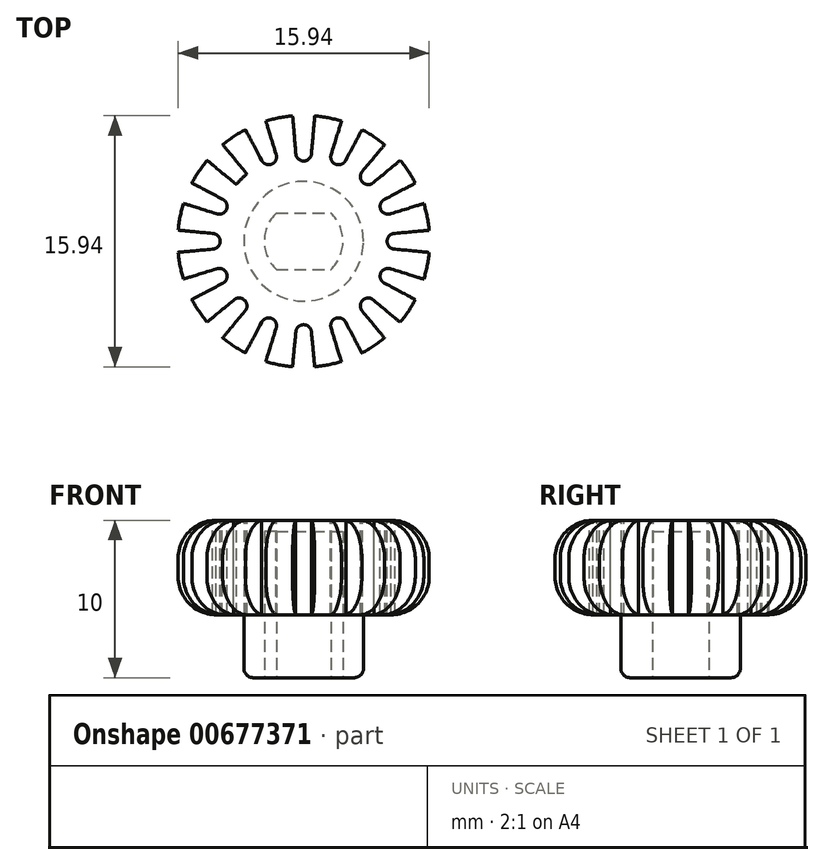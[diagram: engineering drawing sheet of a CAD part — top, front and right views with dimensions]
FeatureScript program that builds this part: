
annotation { "Feature Type Name" : "Feature", "Feature Type Description" : "" }
export const myFeature = defineFeature(function(context is Context, id is Id, definition is map)
    precondition{}
    {
        {
            var Q0;
            Q0=qCreatedBy(makeId("Front.planeOp"),FACE);
            var sketch = newSketch(context, id + "F0", { "sketchPlane" : qUnion([Q0])});
            skLineSegment(sketch, "E0", {"start": v(0, 0) * mm, "end": v(3.8, 0) * mm});
            skLineSegment(sketch, "E1", {"start": v(3.8, 0) * mm, "end": v(3.8, 4) * mm});
            skLineSegment(sketch, "E2", {"start": v(3.8, 4) * mm, "end": v(5.6, 4) * mm});
            skLineSegment(sketch, "E3", {"start": v(8, 6.4) * mm, "end": v(8, 7.6) * mm});
            skLineSegment(sketch, "E4", {"start": v(5.6, 10) * mm, "end": v(0, 10) * mm});
            skLineSegment(sketch, "E5", {"start": v(0, 10) * mm, "end": v(0, 0) * mm});
            skPoint(sketch, "E6.visualSharp", {"position": v(8, 10) * mm});
            skArc(sketch, "E6.filletArc", {"start": v(8, 7.6) * mm, "mid": v(7.3, 9.3) * mm, "end": v(5.6, 10) * mm});
            skPoint(sketch, "E7.visualSharp", {"position": v(8, 4) * mm});
            skArc(sketch, "E7.filletArc", {"start": v(5.6, 4) * mm, "mid": v(7.3, 4.7) * mm, "end": v(8, 6.4) * mm});
            skSolve(sketch);
        }
        {
            var Q0;
            Q0=makeQuery(id+"F0.imprint","IMPRINT",FACE,{"disambiguationData":[TD([[makeQuery(id+"F0.imprint","IMPRINT",EDGE,{"derivedFrom":sQuery(id+"F0.wireOp",EDGE,"E0")}),1.0]])]});
            var Q1;
            Q1=sQuery(id+"F0.wireOp",EDGE,"E5");
            revolve(context, id + "F1", {"entities" : qUnion([Q0]), "axis" : qUnion([Q1]), "revolveType" : RevolveType.FULL});
        }
        {
            var Q0;
            Q0=makeQuery(id+"F1.opRevolve","SWEPT_FACE",FACE,{"disambiguationData":[OSD([sQuery(id+"F0.wireOp",EDGE,"E0")])]});
            var sketch = newSketch(context, id + "F2", { "sketchPlane" : qUnion([Q0])});
            skLineSegment(sketch, "E8", {"start": v(-1.73, 1.8) * mm, "end": v(1.73, 1.8) * mm});
            skLineSegment(sketch, "E9", {"start": v(-1.73, -1.8) * mm, "end": v(1.73, -1.8) * mm});
            skArc(sketch, "E10", {"start": v(-1.73, 1.8) * mm, "mid": v(-2.5, 0) * mm, "end": v(-1.73, -1.8) * mm});
            skArc(sketch, "E11.trimOffspring", {"start": v(1.73, -1.8) * mm, "mid": v(2.5, 0) * mm, "end": v(1.73, 1.8) * mm});
            skPoint(sketch, "E12.orphan", {"position": v(3.04, 1.8) * mm});
            skPoint(sketch, "E13.orphan", {"position": v(2.98, -1.8) * mm});
            skSolve(sketch);
        }
        {
            var Q0;
            Q0=makeQuery(id+"F2.imprint","IMPRINT",FACE,{"disambiguationData":[TD([[makeQuery(id+"F2.imprint","IMPRINT",EDGE,{"derivedFrom":sQuery(id+"F2.wireOp",EDGE,"E8")}),-1.0]])]});
            extrude(context, id + "F3", {"entities" : qUnion([Q0]), "operationType" : NewBodyOperationType.REMOVE, "oppositeDirection" : true, "depth" : 9.3 * mm, "offsetDistance" : 25 * mm});
        }
        {
            var Q0;
            Q0=makeQuery(id+"F1.opRevolve","SWEPT_FACE",FACE,{"disambiguationData":[OSD([sQuery(id+"F0.wireOp",EDGE,"E4")])]});
            var sketch = newSketch(context, id + "F4", { "sketchPlane" : qUnion([Q0])});
            skLineSegment(sketch, "E14", {"start": v(-0.7, 7.97) * mm, "end": v(-0.5, 5.6) * mm});
            skArc(sketch, "E15", {"start": v(-0.5, 5.6) * mm, "mid": v(0, 5.1) * mm, "end": v(0.5, 5.6) * mm});
            skPoint(sketch, "E16.orphan", {"position": v(0.5, 5.6) * mm});
            skLineSegment(sketch, "E17", {"start": v(0.5, 5.6) * mm, "end": v(0.7, 7.97) * mm});
            skPoint(sketch, "E18.1.0", {"position": v(-1.76, 5.55) * mm});
            skArc(sketch, "E18.1.1", {"start": v(-2.68, 5.17) * mm, "mid": v(-2.03, 4.9) * mm, "end": v(-1.76, 5.55) * mm});
            skLineSegment(sketch, "E18.1.2", {"start": v(-3.7, 7.1) * mm, "end": v(-2.68, 5.17) * mm});
            skLineSegment(sketch, "E18.1.3", {"start": v(-1.76, 5.55) * mm, "end": v(-2.4, 7.63) * mm});
            skArc(sketch, "E18.1.4", {"start": v(-2.4, 7.63) * mm, "mid": v(-3.06, 7.4) * mm, "end": v(-3.7, 7.1) * mm});
            skPoint(sketch, "E18.2.0", {"position": v(-3.75, 4.45) * mm});
            skArc(sketch, "E18.2.1", {"start": v(-4.45, 3.75) * mm, "mid": v(-3.75, 3.75) * mm, "end": v(-3.75, 4.45) * mm});
            skLineSegment(sketch, "E18.2.2", {"start": v(-6.13, 5.14) * mm, "end": v(-4.45, 3.75) * mm});
            skLineSegment(sketch, "E18.2.3", {"start": v(-3.75, 4.45) * mm, "end": v(-5.14, 6.13) * mm});
            skArc(sketch, "E18.2.4", {"start": v(-5.14, 6.13) * mm, "mid": v(-5.65, 5.66) * mm, "end": v(-6.13, 5.14) * mm});
            skPoint(sketch, "E18.3.0", {"position": v(-5.17, 2.68) * mm});
            skArc(sketch, "E18.3.1", {"start": v(-5.55, 1.76) * mm, "mid": v(-4.9, 2.03) * mm, "end": v(-5.17, 2.68) * mm});
            skLineSegment(sketch, "E18.3.2", {"start": v(-7.63, 2.4) * mm, "end": v(-5.55, 1.76) * mm});
            skLineSegment(sketch, "E18.3.3", {"start": v(-5.17, 2.68) * mm, "end": v(-7.1, 3.7) * mm});
            skArc(sketch, "E18.3.4", {"start": v(-7.1, 3.7) * mm, "mid": v(-7.39, 3.06) * mm, "end": v(-7.63, 2.4) * mm});
            skPoint(sketch, "E18.4.0", {"position": v(-5.8, 0.5) * mm});
            skArc(sketch, "E18.4.1", {"start": v(-5.8, -0.5) * mm, "mid": v(-5.3, 0) * mm, "end": v(-5.8, 0.5) * mm});
            skLineSegment(sketch, "E18.4.2", {"start": v(-7.97, -0.7) * mm, "end": v(-5.8, -0.5) * mm});
            skLineSegment(sketch, "E18.4.3", {"start": v(-5.8, 0.5) * mm, "end": v(-7.97, 0.7) * mm});
            skArc(sketch, "E18.4.4", {"start": v(-7.97, 0.7) * mm, "mid": v(-8, 0) * mm, "end": v(-7.97, -0.7) * mm});
            skPoint(sketch, "E18.5.0", {"position": v(-5.55, -1.76) * mm});
            skArc(sketch, "E18.5.1", {"start": v(-5.17, -2.68) * mm, "mid": v(-4.9, -2.03) * mm, "end": v(-5.55, -1.76) * mm});
            skLineSegment(sketch, "E18.5.2", {"start": v(-7.1, -3.7) * mm, "end": v(-5.17, -2.68) * mm});
            skLineSegment(sketch, "E18.5.3", {"start": v(-5.55, -1.76) * mm, "end": v(-7.63, -2.4) * mm});
            skArc(sketch, "E18.5.4", {"start": v(-7.63, -2.4) * mm, "mid": v(-7.4, -3.06) * mm, "end": v(-7.1, -3.7) * mm});
            skPoint(sketch, "E18.6.0", {"position": v(-4.45, -3.75) * mm});
            skArc(sketch, "E18.6.1", {"start": v(-3.75, -4.45) * mm, "mid": v(-3.75, -3.75) * mm, "end": v(-4.45, -3.75) * mm});
            skLineSegment(sketch, "E18.6.2", {"start": v(-5.14, -6.13) * mm, "end": v(-3.75, -4.45) * mm});
            skLineSegment(sketch, "E18.6.3", {"start": v(-4.45, -3.75) * mm, "end": v(-6.13, -5.14) * mm});
            skArc(sketch, "E18.6.4", {"start": v(-6.13, -5.14) * mm, "mid": v(-5.66, -5.65) * mm, "end": v(-5.14, -6.13) * mm});
            skPoint(sketch, "E18.7.0", {"position": v(-2.68, -5.17) * mm});
            skArc(sketch, "E18.7.1", {"start": v(-1.76, -5.55) * mm, "mid": v(-2.03, -4.9) * mm, "end": v(-2.68, -5.17) * mm});
            skLineSegment(sketch, "E18.7.2", {"start": v(-2.4, -7.63) * mm, "end": v(-1.76, -5.55) * mm});
            skLineSegment(sketch, "E18.7.3", {"start": v(-2.68, -5.17) * mm, "end": v(-3.7, -7.1) * mm});
            skArc(sketch, "E18.7.4", {"start": v(-3.7, -7.1) * mm, "mid": v(-3.06, -7.39) * mm, "end": v(-2.4, -7.63) * mm});
            skPoint(sketch, "E18.8.0", {"position": v(-0.5, -5.8) * mm});
            skArc(sketch, "E18.8.1", {"start": v(0.5, -5.8) * mm, "mid": v(0, -5.3) * mm, "end": v(-0.5, -5.8) * mm});
            skLineSegment(sketch, "E18.8.2", {"start": v(0.7, -7.97) * mm, "end": v(0.5, -5.8) * mm});
            skLineSegment(sketch, "E18.8.3", {"start": v(-0.5, -5.8) * mm, "end": v(-0.7, -7.97) * mm});
            skArc(sketch, "E18.8.4", {"start": v(-0.7, -7.97) * mm, "mid": v(0, -8) * mm, "end": v(0.7, -7.97) * mm});
            skPoint(sketch, "E18.9.0", {"position": v(1.76, -5.55) * mm});
            skArc(sketch, "E18.9.1", {"start": v(2.68, -5.17) * mm, "mid": v(2.03, -4.9) * mm, "end": v(1.76, -5.55) * mm});
            skLineSegment(sketch, "E18.9.2", {"start": v(3.7, -7.1) * mm, "end": v(2.68, -5.17) * mm});
            skLineSegment(sketch, "E18.9.3", {"start": v(1.76, -5.55) * mm, "end": v(2.4, -7.63) * mm});
            skArc(sketch, "E18.9.4", {"start": v(2.4, -7.63) * mm, "mid": v(3.06, -7.4) * mm, "end": v(3.7, -7.1) * mm});
            skPoint(sketch, "E18.10.0", {"position": v(3.75, -4.45) * mm});
            skArc(sketch, "E18.10.1", {"start": v(4.45, -3.75) * mm, "mid": v(3.75, -3.75) * mm, "end": v(3.75, -4.45) * mm});
            skLineSegment(sketch, "E18.10.2", {"start": v(6.13, -5.14) * mm, "end": v(4.45, -3.75) * mm});
            skLineSegment(sketch, "E18.10.3", {"start": v(3.75, -4.45) * mm, "end": v(5.14, -6.13) * mm});
            skArc(sketch, "E18.10.4", {"start": v(5.14, -6.13) * mm, "mid": v(5.65, -5.66) * mm, "end": v(6.13, -5.14) * mm});
            skPoint(sketch, "E18.11.0", {"position": v(5.17, -2.68) * mm});
            skArc(sketch, "E18.11.1", {"start": v(5.55, -1.76) * mm, "mid": v(4.9, -2.03) * mm, "end": v(5.17, -2.68) * mm});
            skLineSegment(sketch, "E18.11.2", {"start": v(7.63, -2.4) * mm, "end": v(5.55, -1.76) * mm});
            skLineSegment(sketch, "E18.11.3", {"start": v(5.17, -2.68) * mm, "end": v(7.1, -3.7) * mm});
            skArc(sketch, "E18.11.4", {"start": v(7.1, -3.7) * mm, "mid": v(7.39, -3.06) * mm, "end": v(7.63, -2.4) * mm});
            skPoint(sketch, "E18.12.0", {"position": v(5.8, -0.5) * mm});
            skArc(sketch, "E18.12.1", {"start": v(5.8, 0.5) * mm, "mid": v(5.3, 0) * mm, "end": v(5.8, -0.5) * mm});
            skLineSegment(sketch, "E18.12.2", {"start": v(7.97, 0.7) * mm, "end": v(5.8, 0.5) * mm});
            skLineSegment(sketch, "E18.12.3", {"start": v(5.8, -0.5) * mm, "end": v(7.97, -0.7) * mm});
            skArc(sketch, "E18.12.4", {"start": v(7.97, -0.7) * mm, "mid": v(8, 0) * mm, "end": v(7.97, 0.7) * mm});
            skPoint(sketch, "E18.13.0", {"position": v(5.55, 1.76) * mm});
            skArc(sketch, "E18.13.1", {"start": v(5.17, 2.68) * mm, "mid": v(4.9, 2.03) * mm, "end": v(5.55, 1.76) * mm});
            skLineSegment(sketch, "E18.13.2", {"start": v(7.1, 3.7) * mm, "end": v(5.17, 2.68) * mm});
            skLineSegment(sketch, "E18.13.3", {"start": v(5.55, 1.76) * mm, "end": v(7.63, 2.4) * mm});
            skArc(sketch, "E18.13.4", {"start": v(7.63, 2.4) * mm, "mid": v(7.4, 3.06) * mm, "end": v(7.1, 3.7) * mm});
            skPoint(sketch, "E18.14.0", {"position": v(4.45, 3.75) * mm});
            skArc(sketch, "E18.14.1", {"start": v(3.75, 4.45) * mm, "mid": v(3.75, 3.75) * mm, "end": v(4.45, 3.75) * mm});
            skLineSegment(sketch, "E18.14.2", {"start": v(5.14, 6.13) * mm, "end": v(3.75, 4.45) * mm});
            skLineSegment(sketch, "E18.14.3", {"start": v(4.45, 3.75) * mm, "end": v(6.13, 5.14) * mm});
            skArc(sketch, "E18.14.4", {"start": v(6.13, 5.14) * mm, "mid": v(5.66, 5.65) * mm, "end": v(5.14, 6.13) * mm});
            skPoint(sketch, "E18.15.0", {"position": v(2.68, 5.17) * mm});
            skArc(sketch, "E18.15.1", {"start": v(1.76, 5.55) * mm, "mid": v(2.03, 4.9) * mm, "end": v(2.68, 5.17) * mm});
            skLineSegment(sketch, "E18.15.2", {"start": v(2.4, 7.63) * mm, "end": v(1.76, 5.55) * mm});
            skLineSegment(sketch, "E18.15.3", {"start": v(2.68, 5.17) * mm, "end": v(3.72, 7.1) * mm});
            skFitSpline(sketch, "E19", {"points": [v(-0.7, 7.97) * mm, v(0, 8) * mm, v(0.7, 7.97) * mm], "startDerivative": vector(1.38, 0.2) * mm, "endDerivative": vector(1.65, -0.24) * mm});
            skFitSpline(sketch, "E20", {"points": [v(2.4, 7.63) * mm, v(2.92, 7.48) * mm, v(3.3, 7.31) * mm, v(3.72, 7.1) * mm], "startDerivative": vector(1.5, -0.38) * mm, "endDerivative": vector(1.28, -0.64) * mm});
            skSolve(sketch);
        }
        {
            var Q0;
            Q0=makeQuery(id+"F3.boolean.opBoolean","COPY",EDGE,{"derivedFrom":makeQuery(id+"F3.opExtrude","CAP_EDGE",EDGE,{"disambiguationData":[OSD([sQuery(id+"F2.wireOp",EDGE,"E11.trimOffspring")])],"isStart":true})});
            var Q1;
            Q1=makeQuery(id+"F3.boolean.opBoolean","COPY",EDGE,{"derivedFrom":makeQuery(id+"F3.opExtrude","CAP_EDGE",EDGE,{"disambiguationData":[OSD([sQuery(id+"F2.wireOp",EDGE,"E9")])],"isStart":true})});
            var Q2;
            Q2=makeQuery(id+"F3.boolean.opBoolean","COPY",EDGE,{"derivedFrom":makeQuery(id+"F3.opExtrude","CAP_EDGE",EDGE,{"disambiguationData":[OSD([sQuery(id+"F2.wireOp",EDGE,"E10")])],"isStart":true})});
            var Q3;
            Q3=makeQuery(id+"F3.boolean.opBoolean","COPY",EDGE,{"derivedFrom":makeQuery(id+"F3.opExtrude","CAP_EDGE",EDGE,{"disambiguationData":[OSD([sQuery(id+"F2.wireOp",EDGE,"E8")])],"isStart":true})});
            var Q4;
            Q4=makeQuery(id+"F1.opRevolve","SWEPT_EDGE",EDGE,{"disambiguationData":[OSD([sQuery(id+"F0.wireOp",EDGE,"E0"),sQuery(id+"F0.wireOp",EDGE,"E1")])]});
            fillet(context, id + "F5", {"entities" : qUnion([Q0, Q1, Q2, Q3, Q4]), "radius" : 0.6 * mm, "tangentPropagation" : true, "allowEdgeOverflow" : false});
        }
        {
            var Q0;
            {var subQ0=sQuery(id+"F4.wireOp",EDGE,"E18.15.1");var subQ1=makeQuery(id+"F1.opRevolve","SWEPT_EDGE",EDGE,{"disambiguationData":[OSD([sQuery(id+"F0.wireOp",EDGE,"E4"),sQuery(id+"F0.wireOp",EDGE,"E6.filletArc")])]});var subQ2=makeQuery(id+"F4.imprint","INTERSECT",VERTEX,{"disambiguationData":[OD(0.0)],"derivedFrom":[subQ1,subQ0]});Q0=makeQuery(id+"F4.imprint","IMPRINT",FACE,{"disambiguationData":[TD([[makeQuery(id+"F4.imprint","IMPRINT",EDGE,{"disambiguationData":[TD([[subQ2,-1.0]])],"derivedFrom":subQ0}),1.0]])]});}
            var Q1;
            {var subQ1=sQuery(id+"F4.wireOp",EDGE,"E18.14.2");Q1=makeQuery(id+"F4.imprint","IMPRINT",FACE,{"disambiguationData":[TD([[makeQuery(id+"F4.imprint","IMPRINT",EDGE,{"derivedFrom":subQ1}),1.0]])]});}
            var Q2;
            {var subQ0=sQuery(id+"F4.wireOp",EDGE,"E18.14.1");var subQ1=makeQuery(id+"F1.opRevolve","SWEPT_EDGE",EDGE,{"disambiguationData":[OSD([sQuery(id+"F0.wireOp",EDGE,"E4"),sQuery(id+"F0.wireOp",EDGE,"E6.filletArc")])]});var subQ2=makeQuery(id+"F4.imprint","INTERSECT",VERTEX,{"disambiguationData":[OD(0.0)],"derivedFrom":[subQ1,subQ0]});Q2=makeQuery(id+"F4.imprint","IMPRINT",FACE,{"disambiguationData":[TD([[makeQuery(id+"F4.imprint","IMPRINT",EDGE,{"disambiguationData":[TD([[subQ2,-1.0]])],"derivedFrom":subQ0}),1.0]])]});}
            var Q3;
            {var subQ5=sQuery(id+"F4.wireOp",EDGE,"E18.13.2");Q3=makeQuery(id+"F4.imprint","IMPRINT",FACE,{"disambiguationData":[TD([[makeQuery(id+"F4.imprint","IMPRINT",EDGE,{"derivedFrom":subQ5}),1.0]])]});}
            var Q4;
            {var subQ0=sQuery(id+"F4.wireOp",EDGE,"E18.13.1");var subQ1=makeQuery(id+"F1.opRevolve","SWEPT_EDGE",EDGE,{"disambiguationData":[OSD([sQuery(id+"F0.wireOp",EDGE,"E4"),sQuery(id+"F0.wireOp",EDGE,"E6.filletArc")])]});var subQ2=makeQuery(id+"F4.imprint","INTERSECT",VERTEX,{"disambiguationData":[OD(0.0)],"derivedFrom":[subQ1,subQ0]});Q4=makeQuery(id+"F4.imprint","IMPRINT",FACE,{"disambiguationData":[TD([[makeQuery(id+"F4.imprint","IMPRINT",EDGE,{"disambiguationData":[TD([[subQ2,-1.0]])],"derivedFrom":subQ0}),1.0]])]});}
            var Q5;
            {var subQ1=sQuery(id+"F4.wireOp",EDGE,"E18.15.2");Q5=makeQuery(id+"F4.imprint","IMPRINT",FACE,{"disambiguationData":[TD([[makeQuery(id+"F4.imprint","IMPRINT",EDGE,{"derivedFrom":subQ1}),1.0]])]});}
            var Q6;
            {var subQ4=sQuery(id+"F4.wireOp",EDGE,"E14");Q6=makeQuery(id+"F4.imprint","IMPRINT",FACE,{"disambiguationData":[TD([[makeQuery(id+"F4.imprint","IMPRINT",EDGE,{"derivedFrom":subQ4}),1.0]])]});}
            var Q7;
            {var subQ0=sQuery(id+"F4.wireOp",EDGE,"E15");var subQ1=makeQuery(id+"F1.opRevolve","SWEPT_EDGE",EDGE,{"disambiguationData":[OSD([sQuery(id+"F0.wireOp",EDGE,"E4"),sQuery(id+"F0.wireOp",EDGE,"E6.filletArc")])]});var subQ2=makeQuery(id+"F4.imprint","INTERSECT",VERTEX,{"disambiguationData":[OD(0.0)],"derivedFrom":[subQ1,subQ0]});Q7=makeQuery(id+"F4.imprint","IMPRINT",FACE,{"disambiguationData":[TD([[makeQuery(id+"F4.imprint","IMPRINT",EDGE,{"disambiguationData":[TD([[subQ2,-1.0]])],"derivedFrom":subQ0}),1.0]])]});}
            var Q8;
            {var subQ1=sQuery(id+"F4.wireOp",EDGE,"E18.1.2");Q8=makeQuery(id+"F4.imprint","IMPRINT",FACE,{"disambiguationData":[TD([[makeQuery(id+"F4.imprint","IMPRINT",EDGE,{"derivedFrom":subQ1}),1.0]])]});}
            var Q9;
            {var subQ0=sQuery(id+"F4.wireOp",EDGE,"E18.1.1");var subQ1=makeQuery(id+"F1.opRevolve","SWEPT_EDGE",EDGE,{"disambiguationData":[OSD([sQuery(id+"F0.wireOp",EDGE,"E4"),sQuery(id+"F0.wireOp",EDGE,"E6.filletArc")])]});var subQ2=makeQuery(id+"F4.imprint","INTERSECT",VERTEX,{"disambiguationData":[OD(0.0)],"derivedFrom":[subQ1,subQ0]});Q9=makeQuery(id+"F4.imprint","IMPRINT",FACE,{"disambiguationData":[TD([[makeQuery(id+"F4.imprint","IMPRINT",EDGE,{"disambiguationData":[TD([[subQ2,-1.0]])],"derivedFrom":subQ0}),1.0]])]});}
            var Q10;
            {var subQ5=sQuery(id+"F4.wireOp",EDGE,"E18.2.2");Q10=makeQuery(id+"F4.imprint","IMPRINT",FACE,{"disambiguationData":[TD([[makeQuery(id+"F4.imprint","IMPRINT",EDGE,{"derivedFrom":subQ5}),1.0]])]});}
            var Q11;
            {var subQ1=sQuery(id+"F4.wireOp",EDGE,"E18.3.2");Q11=makeQuery(id+"F4.imprint","IMPRINT",FACE,{"disambiguationData":[TD([[makeQuery(id+"F4.imprint","IMPRINT",EDGE,{"derivedFrom":subQ1}),1.0]])]});}
            var Q12;
            {var subQ1=sQuery(id+"F4.wireOp",EDGE,"E18.4.2");Q12=makeQuery(id+"F4.imprint","IMPRINT",FACE,{"disambiguationData":[TD([[makeQuery(id+"F4.imprint","IMPRINT",EDGE,{"derivedFrom":subQ1}),1.0]])]});}
            var Q13;
            {var subQ0=sQuery(id+"F4.wireOp",EDGE,"E18.12.1");var subQ1=makeQuery(id+"F1.opRevolve","SWEPT_EDGE",EDGE,{"disambiguationData":[OSD([sQuery(id+"F0.wireOp",EDGE,"E4"),sQuery(id+"F0.wireOp",EDGE,"E6.filletArc")])]});var subQ2=makeQuery(id+"F4.imprint","INTERSECT",VERTEX,{"disambiguationData":[OD(0.0)],"derivedFrom":[subQ1,subQ0]});Q13=makeQuery(id+"F4.imprint","IMPRINT",FACE,{"disambiguationData":[TD([[makeQuery(id+"F4.imprint","IMPRINT",EDGE,{"disambiguationData":[TD([[subQ2,-1.0]])],"derivedFrom":subQ0}),1.0]])]});}
            var Q14;
            {var subQ1=sQuery(id+"F4.wireOp",EDGE,"E18.11.2");Q14=makeQuery(id+"F4.imprint","IMPRINT",FACE,{"disambiguationData":[TD([[makeQuery(id+"F4.imprint","IMPRINT",EDGE,{"derivedFrom":subQ1}),1.0]])]});}
            var Q15;
            {var subQ0=sQuery(id+"F4.wireOp",EDGE,"E18.11.1");var subQ1=makeQuery(id+"F1.opRevolve","SWEPT_EDGE",EDGE,{"disambiguationData":[OSD([sQuery(id+"F0.wireOp",EDGE,"E4"),sQuery(id+"F0.wireOp",EDGE,"E6.filletArc")])]});var subQ2=makeQuery(id+"F4.imprint","INTERSECT",VERTEX,{"disambiguationData":[OD(0.0)],"derivedFrom":[subQ1,subQ0]});Q15=makeQuery(id+"F4.imprint","IMPRINT",FACE,{"disambiguationData":[TD([[makeQuery(id+"F4.imprint","IMPRINT",EDGE,{"disambiguationData":[TD([[subQ2,-1.0]])],"derivedFrom":subQ0}),1.0]])]});}
            var Q16;
            {var subQ1=sQuery(id+"F4.wireOp",EDGE,"E18.12.2");Q16=makeQuery(id+"F4.imprint","IMPRINT",FACE,{"disambiguationData":[TD([[makeQuery(id+"F4.imprint","IMPRINT",EDGE,{"derivedFrom":subQ1}),1.0]])]});}
            var Q17;
            {var subQ0=sQuery(id+"F4.wireOp",EDGE,"E18.10.1");var subQ1=makeQuery(id+"F1.opRevolve","SWEPT_EDGE",EDGE,{"disambiguationData":[OSD([sQuery(id+"F0.wireOp",EDGE,"E4"),sQuery(id+"F0.wireOp",EDGE,"E6.filletArc")])]});var subQ2=makeQuery(id+"F4.imprint","INTERSECT",VERTEX,{"disambiguationData":[OD(0.0)],"derivedFrom":[subQ1,subQ0]});Q17=makeQuery(id+"F4.imprint","IMPRINT",FACE,{"disambiguationData":[TD([[makeQuery(id+"F4.imprint","IMPRINT",EDGE,{"disambiguationData":[TD([[subQ2,-1.0]])],"derivedFrom":subQ0}),1.0]])]});}
            var Q18;
            {var subQ1=sQuery(id+"F4.wireOp",EDGE,"E18.9.2");Q18=makeQuery(id+"F4.imprint","IMPRINT",FACE,{"disambiguationData":[TD([[makeQuery(id+"F4.imprint","IMPRINT",EDGE,{"derivedFrom":subQ1}),1.0]])]});}
            var Q19;
            {var subQ0=sQuery(id+"F4.wireOp",EDGE,"E18.9.1");var subQ1=makeQuery(id+"F1.opRevolve","SWEPT_EDGE",EDGE,{"disambiguationData":[OSD([sQuery(id+"F0.wireOp",EDGE,"E4"),sQuery(id+"F0.wireOp",EDGE,"E6.filletArc")])]});var subQ2=makeQuery(id+"F4.imprint","INTERSECT",VERTEX,{"disambiguationData":[OD(0.0)],"derivedFrom":[subQ1,subQ0]});Q19=makeQuery(id+"F4.imprint","IMPRINT",FACE,{"disambiguationData":[TD([[makeQuery(id+"F4.imprint","IMPRINT",EDGE,{"disambiguationData":[TD([[subQ2,-1.0]])],"derivedFrom":subQ0}),1.0]])]});}
            var Q20;
            {var subQ1=sQuery(id+"F4.wireOp",EDGE,"E18.8.2");Q20=makeQuery(id+"F4.imprint","IMPRINT",FACE,{"disambiguationData":[TD([[makeQuery(id+"F4.imprint","IMPRINT",EDGE,{"derivedFrom":subQ1}),1.0]])]});}
            var Q21;
            {var subQ0=sQuery(id+"F4.wireOp",EDGE,"E18.8.1");var subQ1=makeQuery(id+"F1.opRevolve","SWEPT_EDGE",EDGE,{"disambiguationData":[OSD([sQuery(id+"F0.wireOp",EDGE,"E4"),sQuery(id+"F0.wireOp",EDGE,"E6.filletArc")])]});var subQ2=makeQuery(id+"F4.imprint","INTERSECT",VERTEX,{"disambiguationData":[OD(0.0)],"derivedFrom":[subQ1,subQ0]});Q21=makeQuery(id+"F4.imprint","IMPRINT",FACE,{"disambiguationData":[TD([[makeQuery(id+"F4.imprint","IMPRINT",EDGE,{"disambiguationData":[TD([[subQ2,-1.0]])],"derivedFrom":subQ0}),1.0]])]});}
            var Q22;
            {var subQ1=sQuery(id+"F4.wireOp",EDGE,"E18.7.2");Q22=makeQuery(id+"F4.imprint","IMPRINT",FACE,{"disambiguationData":[TD([[makeQuery(id+"F4.imprint","IMPRINT",EDGE,{"derivedFrom":subQ1}),1.0]])]});}
            var Q23;
            {var subQ0=sQuery(id+"F4.wireOp",EDGE,"E18.7.1");var subQ1=makeQuery(id+"F1.opRevolve","SWEPT_EDGE",EDGE,{"disambiguationData":[OSD([sQuery(id+"F0.wireOp",EDGE,"E4"),sQuery(id+"F0.wireOp",EDGE,"E6.filletArc")])]});var subQ2=makeQuery(id+"F4.imprint","INTERSECT",VERTEX,{"disambiguationData":[OD(0.0)],"derivedFrom":[subQ1,subQ0]});Q23=makeQuery(id+"F4.imprint","IMPRINT",FACE,{"disambiguationData":[TD([[makeQuery(id+"F4.imprint","IMPRINT",EDGE,{"disambiguationData":[TD([[subQ2,-1.0]])],"derivedFrom":subQ0}),1.0]])]});}
            var Q24;
            {var subQ1=sQuery(id+"F4.wireOp",EDGE,"E18.6.2");Q24=makeQuery(id+"F4.imprint","IMPRINT",FACE,{"disambiguationData":[TD([[makeQuery(id+"F4.imprint","IMPRINT",EDGE,{"derivedFrom":subQ1}),1.0]])]});}
            var Q25;
            {var subQ1=sQuery(id+"F4.wireOp",EDGE,"E18.5.2");Q25=makeQuery(id+"F4.imprint","IMPRINT",FACE,{"disambiguationData":[TD([[makeQuery(id+"F4.imprint","IMPRINT",EDGE,{"derivedFrom":subQ1}),1.0]])]});}
            var Q26;
            {var subQ1=sQuery(id+"F4.wireOp",EDGE,"E18.10.2");Q26=makeQuery(id+"F4.imprint","IMPRINT",FACE,{"disambiguationData":[TD([[makeQuery(id+"F4.imprint","IMPRINT",EDGE,{"derivedFrom":subQ1}),1.0]])]});}
            var Q27;
            {var subQ0=sQuery(id+"F4.wireOp",EDGE,"E18.3.1");var subQ1=makeQuery(id+"F1.opRevolve","SWEPT_EDGE",EDGE,{"disambiguationData":[OSD([sQuery(id+"F0.wireOp",EDGE,"E4"),sQuery(id+"F0.wireOp",EDGE,"E6.filletArc")])]});var subQ2=makeQuery(id+"F4.imprint","INTERSECT",VERTEX,{"disambiguationData":[OD(0.0)],"derivedFrom":[subQ1,subQ0]});Q27=makeQuery(id+"F4.imprint","IMPRINT",FACE,{"disambiguationData":[TD([[makeQuery(id+"F4.imprint","IMPRINT",EDGE,{"disambiguationData":[TD([[subQ2,-1.0]])],"derivedFrom":subQ0}),1.0]])]});}
            var Q28;
            {var subQ0=sQuery(id+"F4.wireOp",EDGE,"E18.4.1");var subQ1=makeQuery(id+"F1.opRevolve","SWEPT_EDGE",EDGE,{"disambiguationData":[OSD([sQuery(id+"F0.wireOp",EDGE,"E4"),sQuery(id+"F0.wireOp",EDGE,"E6.filletArc")])]});var subQ2=makeQuery(id+"F4.imprint","INTERSECT",VERTEX,{"disambiguationData":[OD(0.0)],"derivedFrom":[subQ1,subQ0]});Q28=makeQuery(id+"F4.imprint","IMPRINT",FACE,{"disambiguationData":[TD([[makeQuery(id+"F4.imprint","IMPRINT",EDGE,{"disambiguationData":[TD([[subQ2,-1.0]])],"derivedFrom":subQ0}),1.0]])]});}
            var Q29;
            {var subQ0=sQuery(id+"F4.wireOp",EDGE,"E18.5.1");var subQ1=makeQuery(id+"F1.opRevolve","SWEPT_EDGE",EDGE,{"disambiguationData":[OSD([sQuery(id+"F0.wireOp",EDGE,"E4"),sQuery(id+"F0.wireOp",EDGE,"E6.filletArc")])]});var subQ2=makeQuery(id+"F4.imprint","INTERSECT",VERTEX,{"disambiguationData":[OD(0.0)],"derivedFrom":[subQ1,subQ0]});Q29=makeQuery(id+"F4.imprint","IMPRINT",FACE,{"disambiguationData":[TD([[makeQuery(id+"F4.imprint","IMPRINT",EDGE,{"disambiguationData":[TD([[subQ2,-1.0]])],"derivedFrom":subQ0}),1.0]])]});}
            var Q30;
            {var subQ0=sQuery(id+"F4.wireOp",EDGE,"E18.6.1");var subQ1=makeQuery(id+"F1.opRevolve","SWEPT_EDGE",EDGE,{"disambiguationData":[OSD([sQuery(id+"F0.wireOp",EDGE,"E4"),sQuery(id+"F0.wireOp",EDGE,"E6.filletArc")])]});var subQ2=makeQuery(id+"F4.imprint","INTERSECT",VERTEX,{"disambiguationData":[OD(0.0)],"derivedFrom":[subQ1,subQ0]});Q30=makeQuery(id+"F4.imprint","IMPRINT",FACE,{"disambiguationData":[TD([[makeQuery(id+"F4.imprint","IMPRINT",EDGE,{"disambiguationData":[TD([[subQ2,-1.0]])],"derivedFrom":subQ0}),1.0]])]});}
            extrude(context, id + "F6", {"entities" : qUnion([Q0, Q1, Q2, Q3, Q4, Q5, Q6, Q7, Q8, Q9, Q10, Q11, Q12, Q13, Q14, Q15, Q16, Q17, Q18, Q19, Q20, Q21, Q22, Q23, Q24, Q25, Q26, Q27, Q28, Q29, Q30]), "operationType" : NewBodyOperationType.REMOVE, "oppositeDirection" : true, "depth" : 25 * mm, "offsetDistance" : 25 * mm});
        }
    });
